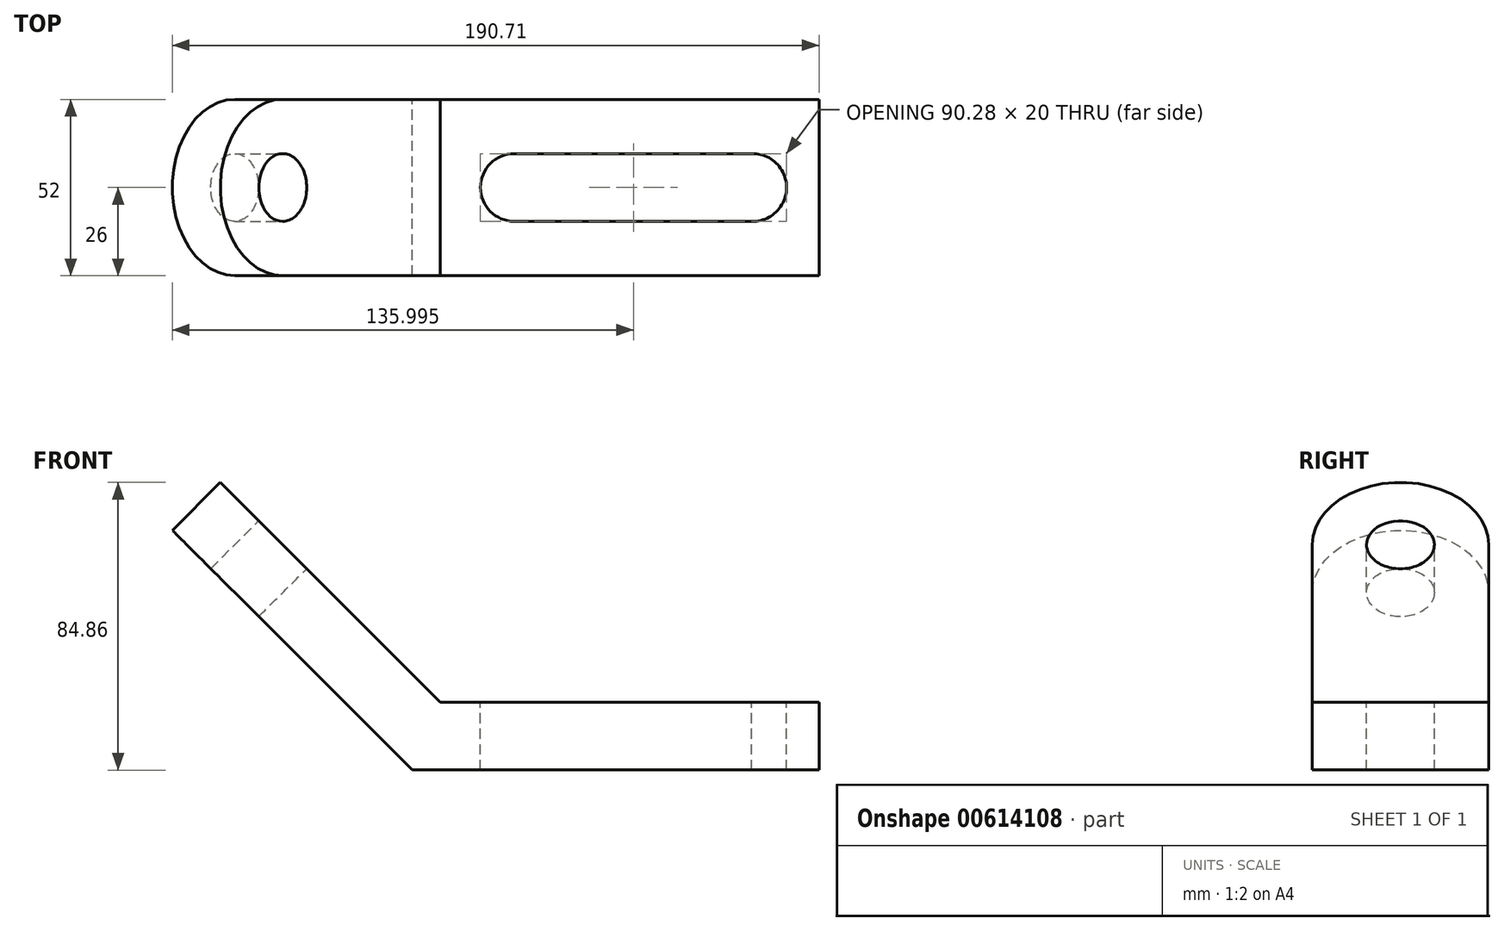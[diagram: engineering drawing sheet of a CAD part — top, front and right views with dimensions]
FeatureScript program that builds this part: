
annotation { "Feature Type Name" : "Feature", "Feature Type Description" : "" }
export const myFeature = defineFeature(function(context is Context, id is Id, definition is map)
    precondition{}
    {
        {
            var Q0;
            Q0=qCreatedBy(makeId("Front.planeOp"),FACE);
            var sketch = newSketch(context, id + "F0", { "sketchPlane" : qUnion([Q0])});
            skLineSegment(sketch, "E0.bottom", {"start": v(-16.96, 18.48) * mm, "end": v(73.04, 18.48) * mm});
            skLineSegment(sketch, "E0.top", {"start": v(-16.96, -1.52) * mm, "end": v(73.04, -1.52) * mm});
            skLineSegment(sketch, "E0.left", {"start": v(-16.96, 18.48) * mm, "end": v(-16.96, -1.52) * mm});
            skLineSegment(sketch, "E0.right", {"start": v(73.04, 18.48) * mm, "end": v(73.04, -1.52) * mm});
            skLineSegment(sketch, "E1.bottom", {"start": v(73.04, 18.48) * mm, "end": v(83.04, 18.48) * mm});
            skLineSegment(sketch, "E1.top", {"start": v(73.04, -1.52) * mm, "end": v(83.04, -1.52) * mm});
            skLineSegment(sketch, "E1.right", {"start": v(83.04, 18.48) * mm, "end": v(83.04, -1.52) * mm});
            skLineSegment(sketch, "E2", {"start": v(-16.96, -1.52) * mm, "end": v(-36.96, -1.52) * mm});
            skLineSegment(sketch, "E3", {"start": v(-36.96, -1.52) * mm, "end": v(-107.67, 69.2) * mm});
            skLineSegment(sketch, "E4", {"start": v(-107.67, 69.2) * mm, "end": v(-93.53, 83.34) * mm});
            skLineSegment(sketch, "E5", {"start": v(-93.53, 83.34) * mm, "end": v(-82.21, 72.02) * mm});
            skLineSegment(sketch, "E6", {"start": v(-82.21, 72.02) * mm, "end": v(-68.07, 57.88) * mm});
            skLineSegment(sketch, "E7", {"start": v(-68.07, 57.88) * mm, "end": v(-28.67, 18.48) * mm});
            skLineSegment(sketch, "E8", {"start": v(-16.96, 18.48) * mm, "end": v(-28.67, 18.48) * mm});
            skSolve(sketch);
        }
        {
            var Q0;
            Q0=makeQuery(id+"F0.imprint","IMPRINT",FACE,{"disambiguationData":[TD([[makeQuery(id+"F0.imprint","IMPRINT",EDGE,{"derivedFrom":sQuery(id+"F0.wireOp",EDGE,"E0.left")}),-1.0]])]});
            var Q1;
            Q1=makeQuery(id+"F0.imprint","IMPRINT",FACE,{"disambiguationData":[TD([[makeQuery(id+"F0.imprint","IMPRINT",EDGE,{"derivedFrom":sQuery(id+"F0.wireOp",EDGE,"E0.bottom")}),-1.0]])]});
            var Q2;
            Q2=makeQuery(id+"F0.imprint","IMPRINT",FACE,{"disambiguationData":[TD([[makeQuery(id+"F0.imprint","IMPRINT",EDGE,{"derivedFrom":sQuery(id+"F0.wireOp",EDGE,"E1.bottom")}),-1.0]])]});
            extrude(context, id + "F1", {"entities" : qUnion([Q0, Q1, Q2]), "depth" : 52 * mm, "offsetDistance" : 25 * mm});
        }
        {
            var Q0;
            Q0=makeQuery(id+"F1.opExtrude","SWEPT_FACE",FACE,{"disambiguationData":[OSD([sQuery(id+"F0.wireOp",EDGE,"E0.bottom"),sQuery(id+"F0.wireOp",EDGE,"E1.bottom"),sQuery(id+"F0.wireOp",EDGE,"E8")])]});
            var sketch = newSketch(context, id + "F2", { "sketchPlane" : qUnion([Q0])});
            skLineSegment(sketch, "E9", {"start": v(73.46, 0) * mm, "end": v(73.46, -26) * mm});
            skLineSegment(sketch, "E10", {"start": v(73.46, -26) * mm, "end": v(0, -26) * mm});
            skLineSegment(sketch, "E11", {"start": v(0, -26) * mm, "end": v(-15.57, -26) * mm});
            skLineSegment(sketch, "E12", {"start": v(-16.81, 0) * mm, "end": v(-16.81, -26) * mm});
            skLineSegment(sketch, "E13", {"start": v(-16.81, -26) * mm, "end": v(-15.57, -26) * mm});
            skLineSegment(sketch, "E14", {"start": v(73.46, -26) * mm, "end": v(52.67, -26) * mm});
            skLineSegment(sketch, "E15", {"start": v(-15.57, -26) * mm, "end": v(-5.57, -26) * mm});
            skLineSegment(sketch, "E16", {"start": v(73.46, -26) * mm, "end": v(63.46, -26) * mm});
            skLineSegment(sketch, "E17", {"start": v(-16.81, -26) * mm, "end": v(-6.81, -26) * mm});
            skLineSegment(sketch, "E18.bottom", {"start": v(-6.81, -26) * mm, "end": v(63.19, -26) * mm});
            skLineSegment(sketch, "E18.top", {"start": v(-6.81, -16) * mm, "end": v(63.19, -16) * mm});
            skLineSegment(sketch, "E18.left", {"start": v(-6.81, -26) * mm, "end": v(-6.81, -16) * mm});
            skLineSegment(sketch, "E18.right", {"start": v(63.19, -26) * mm, "end": v(63.19, -16) * mm});
            skLineSegment(sketch, "E19.bottom", {"start": v(63.19, -26) * mm, "end": v(-6.81, -26) * mm});
            skLineSegment(sketch, "E19.top", {"start": v(63.19, -36) * mm, "end": v(-6.81, -36) * mm});
            skLineSegment(sketch, "E19.left", {"start": v(63.19, -26) * mm, "end": v(63.19, -36) * mm});
            skLineSegment(sketch, "E19.right", {"start": v(-6.81, -26) * mm, "end": v(-6.81, -36) * mm});
            skSolve(sketch);
        }
        {
            var Q0;
            Q0=sQuery(id+"F2.wireOp",VERTEX,"E16.end");
            var Q1;
            Q1=sQuery(id+"F2.wireOp",VERTEX,"E17.end");
            var Q2;
            Q2=makeQuery(id+"F1.opExtrude","SWEPT_BODY",BODY,{"disambiguationData":[OSD([sQuery(id+"F0.wireOp",EDGE,"E0.bottom"),sQuery(id+"F0.wireOp",EDGE,"E0.top"),sQuery(id+"F0.wireOp",EDGE,"E1.bottom"),sQuery(id+"F0.wireOp",EDGE,"E1.top"),sQuery(id+"F0.wireOp",EDGE,"E1.right"),sQuery(id+"F0.wireOp",EDGE,"E2"),sQuery(id+"F0.wireOp",EDGE,"E3"),sQuery(id+"F0.wireOp",EDGE,"E4"),sQuery(id+"F0.wireOp",EDGE,"E5"),sQuery(id+"F0.wireOp",EDGE,"E6"),sQuery(id+"F0.wireOp",EDGE,"E7"),sQuery(id+"F0.wireOp",EDGE,"E8")])]});
            hole(context, id + "F3", {"style" : HoleStyle.SIMPLE, "endStyle" : HoleEndStyle.THROUGH, "holeDiameter" : 20 * mm, "majorDiameter" : 5 * mm, "isTappedThrough" : true, "tappedDepth" : 12 * mm, "tapClearance" : 3, "locations" : qUnion([Q0, Q1]), "scope" : qUnion([Q2])});
        }
        {
            var Q0;
            Q0=makeQuery(id+"F1.opExtrude","SWEPT_FACE",FACE,{"disambiguationData":[OSD([sQuery(id+"F0.wireOp",EDGE,"E5"),sQuery(id+"F0.wireOp",EDGE,"E6"),sQuery(id+"F0.wireOp",EDGE,"E7")])]});
            var sketch = newSketch(context, id + "F4", { "sketchPlane" : qUnion([Q0])});
            skLineSegment(sketch, "E20", {"start": v(-26, 125.06) * mm, "end": v(-26, 109.06) * mm});
            skLineSegment(sketch, "E21", {"start": v(-26, 109.06) * mm, "end": v(-26, 99.06) * mm});
            skSolve(sketch);
        }
        {
            var Q0;
            Q0=sQuery(id+"F4.wireOp",VERTEX,"E21.end");
            var Q1;
            Q1=makeQuery(id+"F1.opExtrude","SWEPT_BODY",BODY,{"disambiguationData":[OSD([sQuery(id+"F0.wireOp",EDGE,"E0.bottom"),sQuery(id+"F0.wireOp",EDGE,"E0.top"),sQuery(id+"F0.wireOp",EDGE,"E1.bottom"),sQuery(id+"F0.wireOp",EDGE,"E1.top"),sQuery(id+"F0.wireOp",EDGE,"E1.right"),sQuery(id+"F0.wireOp",EDGE,"E2"),sQuery(id+"F0.wireOp",EDGE,"E3"),sQuery(id+"F0.wireOp",EDGE,"E4"),sQuery(id+"F0.wireOp",EDGE,"E5"),sQuery(id+"F0.wireOp",EDGE,"E6"),sQuery(id+"F0.wireOp",EDGE,"E7"),sQuery(id+"F0.wireOp",EDGE,"E8")])]});
            hole(context, id + "F5", {"style" : HoleStyle.SIMPLE, "endStyle" : HoleEndStyle.THROUGH, "holeDiameter" : 20 * mm, "majorDiameter" : 5 * mm, "isTappedThrough" : true, "tappedDepth" : 12 * mm, "tapClearance" : 3, "locations" : qUnion([Q0]), "scope" : qUnion([Q1])});
        }
        {
            var Q0;
            Q0=makeQuery(id+"F1.opExtrude","CAP_EDGE",EDGE,{"disambiguationData":[OSD([sQuery(id+"F0.wireOp",EDGE,"E4")])],"isStart":true});
            var Q1;
            Q1=makeQuery(id+"F1.opExtrude","CAP_EDGE",EDGE,{"disambiguationData":[OSD([sQuery(id+"F0.wireOp",EDGE,"E4")])],"isStart":false});
            fillet(context, id + "F6", {"entities" : qUnion([Q0, Q1]), "radius" : 26 * mm, "tangentPropagation" : true, "allowEdgeOverflow" : false});
        }
        {
            var Q0;
            Q0=makeQuery(id+"F2.imprint","IMPRINT",FACE,{"disambiguationData":[TD([[makeQuery(id+"F2.imprint","IMPRINT",EDGE,{"derivedFrom":sQuery(id+"F2.wireOp",EDGE,"E19.top")}),-1.0]])]});
            var Q1;
            Q1=makeQuery(id+"F2.imprint","IMPRINT",FACE,{"disambiguationData":[TD([[makeQuery(id+"F2.imprint","IMPRINT",EDGE,{"derivedFrom":sQuery(id+"F2.wireOp",EDGE,"E18.top")}),-1.0]])]});
            extrude(context, id + "F7", {"entities" : qUnion([Q0, Q1]), "operationType" : NewBodyOperationType.REMOVE, "oppositeDirection" : true, "depth" : 312 * mm, "offsetDistance" : 25 * mm});
        }
    });
